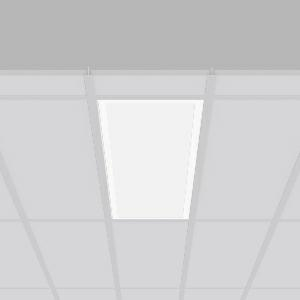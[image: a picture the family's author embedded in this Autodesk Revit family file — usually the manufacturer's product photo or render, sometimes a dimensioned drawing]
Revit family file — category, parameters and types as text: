
# Revit family: sidelite_eco_672377_002_1_07_afe2
name_source: partatom
category: Lighting Fixtures
units: mm (PartAtom-declared; Revit-internal decimal feet)

## family parameters
Cut with Voids When Loaded = No
Host = Face
Light Source = No
Part Type = Normal
Room Calculation Point = No
Round Connector Dimension = Use Diameter
Shared = No

## types (1)
- SIDELITE ECO (1 x LED Modul 840, 3500 lm, 4000)
    Apparent Load = 29 VA
    CIE Flux Codes = 47 79 96 100 100
    Color Rendering = 80
    Color Temperature = 4000
    Default Elevation = 1800 mm
    Description = Series: SIDELITE ECO
Highly economical recessed luminaire with progressive LED technology. For escape route illumination. Frame made of aluminium, powder-coated. Diffuser: plastic, opal. Lightguide and diffuser made of non-yellowing plastic (PMMA). Lateral light emission (RZB SIDELITE technology) for homogeneous light distribution. External driver. Self-contained system with automatic self-test and feedback via DALI bus, only to RZB DALI monitoring system. External driver with simple plug-in locking system. Extended connection cable (1.90 m). 
Colour: white
Length: 1245 mm
Width: 308 mm
Cut-out length: 1220 mm
Cut-out width: 285 mm
Recess height: 160 mm
Luminaire: recess height: 40 mm
Weight: 4.67 kg
Operating mode: maintained power mode
Duration time: 3 h
Lamp: LED
Socket: without socket
Colour temperature: 4000K
Colour rendering index (CRI): 80
System power: 29 W
Rated luminous flux: 3500 lm
Luminous flux, emergency: 520 lm
System power, emergency: -
Control gear: Regulated power supply
Protection class: I
Type of protection: IP 40
    Height = 0 mm  [stored 0 ft]
    Lamp = 1 x LED Modul 840
    Lamp Light Flux = 3500 lm
    Lamp count = 1
    Length = 1245 mm
    Lifetime = 50000 h
    Luminous efficacy = 121 lm/W
    Manufacturer = RZB
    ModVariant = No
    Model = 672377.002.1.07
    Mounting Place = Ceiling
    Mounting Type = Recessed
    Number of Poles = 1
    OnlyDefault = Yes
    Power Factor = 1
    Product Name = SIDELITE ECO
    Product group = Recessed modular luminaires
    ProductGroupID = 406
    Protection Class = Protection class I
    Protection Degree = IP 40
    RLX_Detail_Level = 1
    RLX_Emergency_Light_Flux = 520 lm
    RLX_Emergency_Type = 3
    RLX_Emergency_Type_DB = Yes
    RlxData = <blob elided: 30009 chars, md5=4f3006f5>
    Socket = socket
    Standby Power = 0 W
    System Light Flux = 3500 lm
    System Power = 29 W
    Type Comments = Product without accessories
    Type Image = 312367.002.jpg
    URL = http://relux.com
    VarID = ---
    Voltage = 230 V
    Voltage Range = 220-240 V
    Weight = 0.00 kg
    Width = 308 mm

note: [stored X ft] marks values corroborated as IEEE doubles in the binary element streams (Revit-internal decimal feet)

## geometry (parser evidence)
native form markers: Blend x4, Sweep x11
no freeform markers — native parametric forms only
